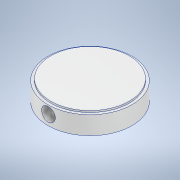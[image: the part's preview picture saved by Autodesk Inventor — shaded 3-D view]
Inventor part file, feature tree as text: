
AUTODESK INVENTOR PART (.ipt)
format: ipt  version: 2020 (Build 240168000, 168)  size: 143,360 bytes
history: native  units: mm
features: sketch x5, hole x3, extrude x2, plane x2
ambient origin geometry x8: Origin, YZ Plane, XZ Plane, XY Plane, X Axis, Y Axis, Z Axis, Center Point
bodies: Solid1 (feature_tree)
feature tree (12):
  extrude  "Extrusion1"  Depth=24.0mm TaperAngle=0.0deg
  plane  "Work Plane1"
  hole  "Hole1"  [1 undecoded]
  hole  "Hole2"  [1 undecoded]
  hole  "Hole3"  [1 undecoded]
  plane  "Work Plane2"
  extrude  "Extrusion4"  Depth=2.0mm
  sketch  "Sketch1"  dims[d0=101.6mm d1=24.0mm d2=0.0mm]
  sketch  "Sketch3"  dims[d7=12.0mm]
  sketch  "Sketch4"  dims[d8=16.5mm d9=6.0mm d10=4.0mm d11=2.0mm d12=90.0deg d13=88.9mm d14=20.594885mm d15=25.0mm]
  sketch  "Sketch5"  dims[d16=25.0mm]
  sketch  "Sketch7"  dims[d17=4.134mm d18=10.0mm d19=4.0mm d20=2.0mm d21=90.0deg d22=14.2mm d23=20.594885mm d24=4.917mm d25=11.0mm d26=4.0mm d27=2.0mm d28=90.0deg d29=12.0mm d30=20.594885mm d31=-88.9mm d35=101.6mm d36=95.0mm d37=2.0mm d38=0.0mm]
note: 3 required parameter values undecoded (feature->parameter linkage not recoverable at this tier; creation-order binding heuristic only, values carry confidence <= 0.55)
